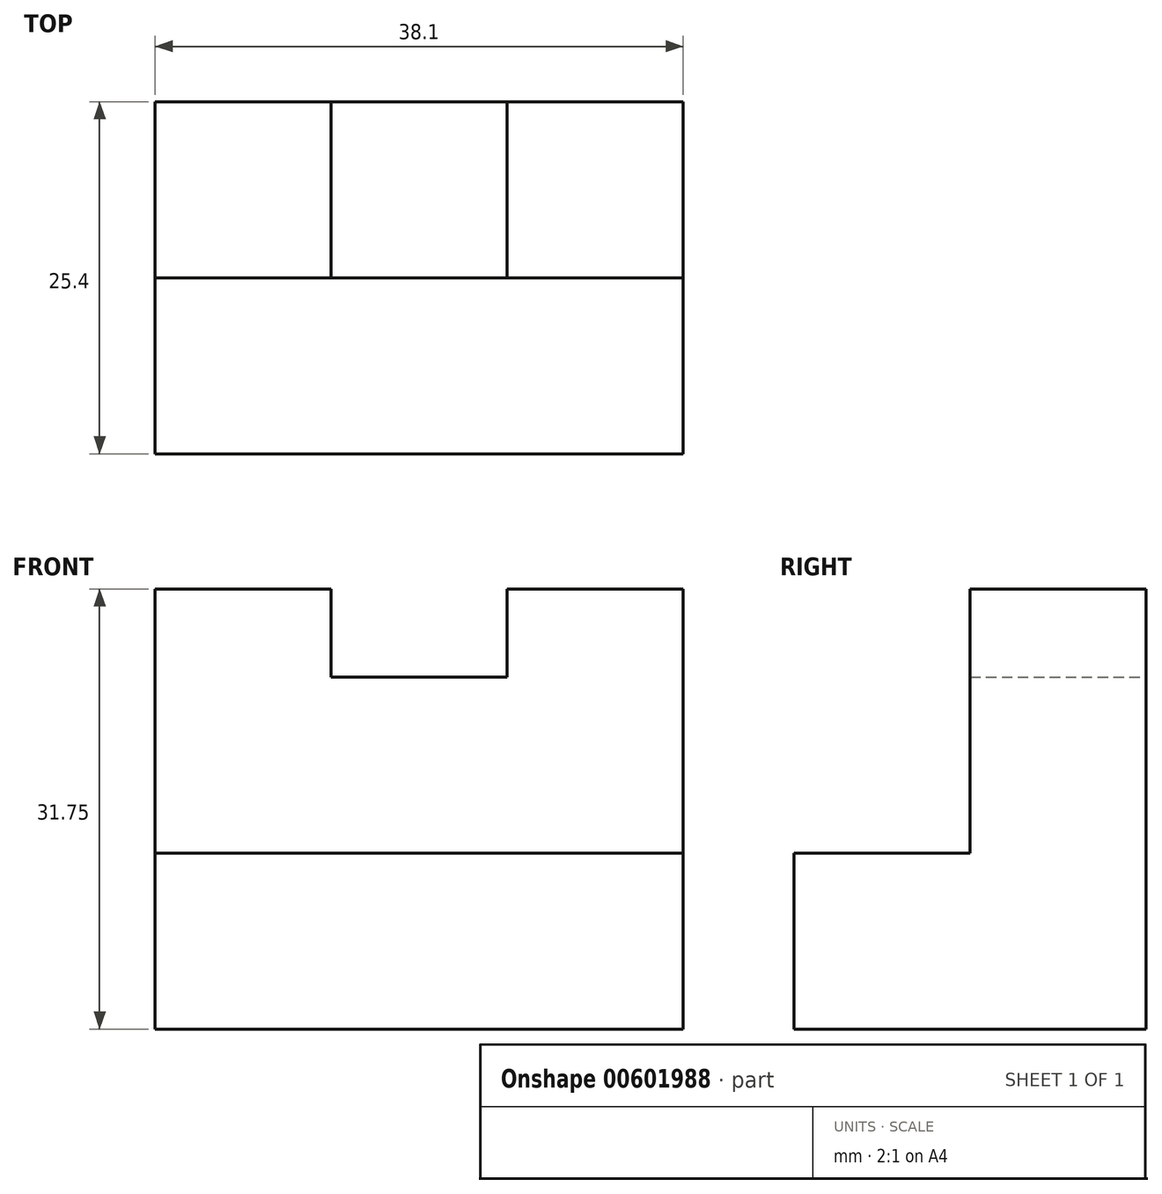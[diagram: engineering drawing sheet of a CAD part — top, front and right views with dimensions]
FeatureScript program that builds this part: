
annotation { "Feature Type Name" : "Feature", "Feature Type Description" : "" }
export const myFeature = defineFeature(function(context is Context, id is Id, definition is map)
    precondition{}
    {
        {
            var Q0;
            Q0=qCreatedBy(makeId("Front.planeOp"),FACE);
            var sketch = newSketch(context, id + "F0", { "sketchPlane" : qUnion([Q0])});
            skLineSegment(sketch, "E0", {"start": v(0, 0) * mm, "end": v(38.1, 0) * mm});
            skLineSegment(sketch, "E1", {"start": v(0, 0) * mm, "end": v(0, 12.7) * mm});
            skLineSegment(sketch, "E2", {"start": v(38.1, 0) * mm, "end": v(38.1, 12.7) * mm});
            skLineSegment(sketch, "E3", {"start": v(0, 12.7) * mm, "end": v(38.1, 12.7) * mm});
            skLineSegment(sketch, "E4", {"start": v(0, 12.7) * mm, "end": v(0, 31.75) * mm});
            skLineSegment(sketch, "E5", {"start": v(38.1, 12.7) * mm, "end": v(38.1, 31.75) * mm});
            skLineSegment(sketch, "E6", {"start": v(0, 31.75) * mm, "end": v(12.7, 31.75) * mm});
            skLineSegment(sketch, "E7", {"start": v(38.1, 31.75) * mm, "end": v(25.4, 31.75) * mm});
            skLineSegment(sketch, "E8", {"start": v(12.7, 31.75) * mm, "end": v(12.7, 25.4) * mm});
            skLineSegment(sketch, "E9", {"start": v(25.4, 31.75) * mm, "end": v(25.4, 25.4) * mm});
            skLineSegment(sketch, "E10", {"start": v(12.7, 25.4) * mm, "end": v(25.4, 25.4) * mm});
            skSolve(sketch);
        }
        {
            var Q0;
            Q0=makeQuery(id+"F0.imprint","IMPRINT",FACE,{"disambiguationData":[TD([[makeQuery(id+"F0.imprint","IMPRINT",EDGE,{"derivedFrom":sQuery(id+"F0.wireOp",EDGE,"E3")}),1.0]])]});
            var sketch = newSketch(context, id + "F1", { "sketchPlane" : qUnion([Q0])});
            skSolve(sketch);
        }
        {
            var Q0;
            Q0 = qSketchRegion(id + "F1", true);
            var Q1;
            Q1=makeQuery(id+"F0.imprint","IMPRINT",FACE,{"disambiguationData":[TD([[makeQuery(id+"F0.imprint","IMPRINT",EDGE,{"derivedFrom":sQuery(id+"F0.wireOp",EDGE,"E0")}),1.0]])]});
            var Q2;
            Q2=makeQuery(id+"F0.imprint","IMPRINT",FACE,{"disambiguationData":[TD([[makeQuery(id+"F0.imprint","IMPRINT",EDGE,{"derivedFrom":sQuery(id+"F0.wireOp",EDGE,"E3")}),1.0]])]});
            extrude(context, id + "F2", {"entities" : qUnion([Q0, Q1, Q2]), "depth" : 12.7 * mm, "offsetDistance" : 25.4 * mm});
        }
        {
            var Q0;
            Q0=qCreatedBy(makeId("Front.planeOp"),FACE);
            var sketch = newSketch(context, id + "F3", { "sketchPlane" : qUnion([Q0])});
            skLineSegment(sketch, "E11", {"start": v(0, 0) * mm, "end": v(0, 12.7) * mm});
            skLineSegment(sketch, "E12", {"start": v(0, 0) * mm, "end": v(38.1, 0) * mm});
            skLineSegment(sketch, "E13", {"start": v(38.1, 0) * mm, "end": v(38.1, 12.7) * mm});
            skLineSegment(sketch, "E14", {"start": v(0, 12.7) * mm, "end": v(38.1, 12.7) * mm});
            skSolve(sketch);
        }
        {
            var Q0;
            Q0 = qSketchRegion(id + "F3", true);
            extrude(context, id + "F4", {"entities" : qUnion([Q0]), "operationType" : NewBodyOperationType.ADD, "depth" : 25.4 * mm, "offsetDistance" : 25.4 * mm});
        }
    });
